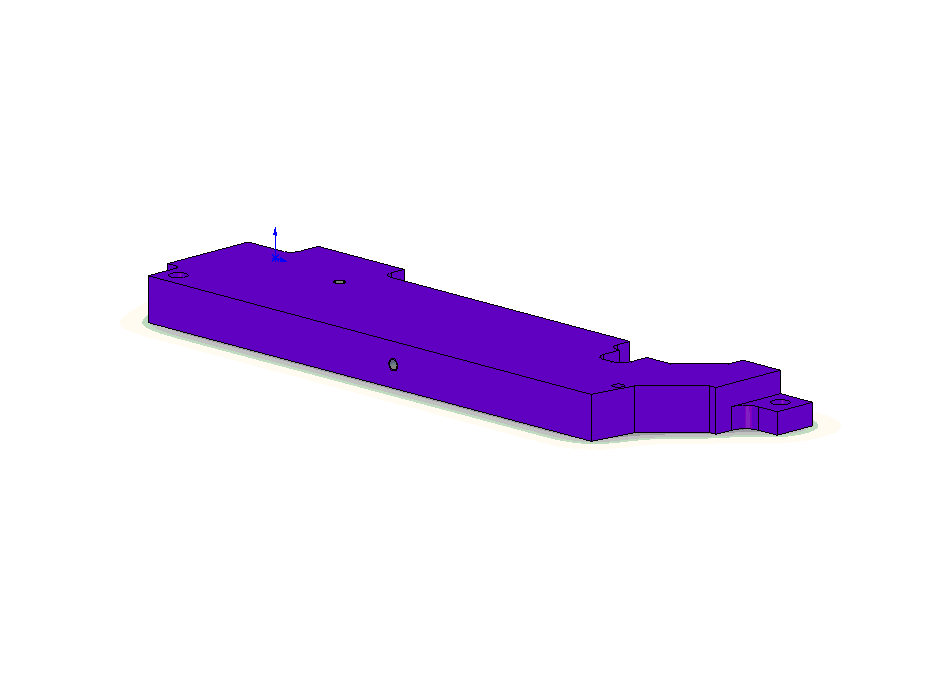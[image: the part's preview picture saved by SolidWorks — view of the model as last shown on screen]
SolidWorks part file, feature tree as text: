
SOLIDWORKS PART (.sldprt)
format: sldprt  version: not decoded by parser v0  size: 1,095,680 bytes
history: native  units: mm
features: sketch x17, cut_extrude x8, hole x4, thread x3, material x1, extrude x1, fillet x1 (+12 scaffold rows collapsed)
feature tree (47):
  scaffold x12  (default folders/planes/origin — collapsed)
  material  "Material <not specified>"
  sketch  "Sketch1"  dims[D1=16.0mm D2=250.0mm D3=~250.008967mm]
  extrude  "Base-Extrude"  Depth=65mm
  sketch  "Sketch3"  dims[c1.D3=20.0mm c1.D4=4.0mm c1.D6=4.0mm c1.D1=15.0mm c1.D2=60.0mm c2.D1=45.0mm c2.D2=18.0mm c3.D1=45.0mm c3.D3=28.0mm c3.D4=15.0mm c4.D1=7.0mm c4.D4=65.0mm c5.D1=~29.08854mm c6.D1=6.0deg c6.D2=16.0mm c6.D4=15.0mm c6.D5=34.595mm c6.D6=435.0mm c6.D7=~364.989602mm c7.D2=400.0mm c7.D7=30.0mm c7.D1=400.0mm c8.D1=~8.616174deg c9.D1=435.0mm c10.D1=8.5deg c11.D1=~45.694142mm c12.D1=81.5deg c12.D2=38.0mm c12.D3=35.0mm c12.D4=18.0mm c12.D5=~25.347536mm c13.D5=45.0deg]
  cut_extrude  "Access for Blade Clamp Bolts"  [1 undecoded]
  sketch  "Sketch6"  dims[c1.D5=4.0mm c1.D6=4.0mm c1.D1=100.0mm c1.D2=10.0mm c1.D3=~45.280213mm c2.D3=90.0deg c3.D3=10.0mm c3.D4=40.0mm c3.D5=20.0mm c4.D3=40.0mm c4.D4=10.0mm]
  cut_extrude  "Cut-Extrude2"  [1 undecoded]
  sketch  "Sketch7"  dims[c1.D2=4.0mm c1.D4=4.0mm c2.D2=4.0mm c2.D1=32.5mm c2.D3=10.0mm c2.D4=~35.410935mm c2.D5=42.5mm c2.D6=~16.138316mm c3.D6=45.0deg c3.D7=5.0mm c3.D2=29.0mm]
  cut_extrude  "Cut-Extrude3"  [1 undecoded]
  hole  "1/4 Clearance Hole1"  Diameter=6.5278mm Depth=16mm
  sketch  "3DSketch2"  dims[c1.D1=7.5mm c1.D2=~9.694641mm c1.D7=7.5mm c1.D3=12.5mm c1.D4=12.5mm c1.D5=6.0mm c1.D6=7.5mm c2.D2=7.5mm c2.D7=7.5mm c2.D8=7.5mm]
  sketch  "Sketch10"  dims[hole-wizard template sketch: 60 standard entries collapsed; hole parameters kept: c18.Thru Hole Depth=16.0mm]
  sketch  "Sketch11"  dims[D3=2.0mm D4=2.0mm D1=6.0mm D2=12.5mm D5=6.0mm D6=15.0mm]
  cut_extrude  "Cut-Extrude4"  [1 undecoded]
  sketch  "Sketch12"  dims[D2=4.0mm D1=20.0mm]
  cut_extrude  "Cut-Extrude5"  Depth=8mm
  hole  "#8-32 Tapped Hole1"  Diameter=3.4544mm Depth=16mm
  sketch  "3DSketch3"  dims[D1=39.0mm D2=194.0mm]
  sketch  "Sketch13"  dims[hole-wizard template sketch: 60 standard entries collapsed; hole parameters kept: c18.Thru Tap Drill Depth=16.0mm]
  thread  "Cosmetic Thread1"  Diameter=8.3312mm  [1 undecoded]
  hole  "#8-32 Tapped Hole2"  Diameter=3.4544mm Depth=12.2936mm
  sketch  "Sketch15"  dims[D1=130.0mm D2=8.0mm]
  sketch  "Sketch14"  dims[hole-wizard template sketch: 47 standard entries collapsed; hole parameters kept: c15.Tap Drill Depth=12.2936mm c15.D3=~14.816244mm c15.Drill Angle=118.0deg]
  thread  "Cosmetic Thread2"  Diameter=8.3312mm  [1 undecoded]
  hole  "#8-32 Tapped Hole3"  Diameter=3.4544mm Depth=16mm
  sketch  "Sketch18"  dims[D1=38.1mm D2=63.5mm]
  sketch  "Sketch19"  dims[hole-wizard template sketch: 60 standard entries collapsed; hole parameters kept: c18.Thru Tap Drill Depth=16.0mm]
  thread  "Cosmetic Thread3"  Diameter=8.3312mm  [1 undecoded]
  sketch  "Sketch20"  dims[D1=15.0mm]
  cut_extrude  "Cut-Extrude6"  [1 undecoded]
  sketch  "Sketch22"  dims[D1=6.35mm D2=12.7mm D3=4.85mm]
  cut_extrude  "Cut-Extrude8"  Depth=9.525mm
  sketch  "Sketch23"  dims[D1=12.0mm D2=13.5mm]
  cut_extrude  "Cut-Extrude9"  [1 undecoded]
  fillet  "Fillet1"  Radius=4.5mm
decode coverage: 28 of 34 modeling features carry decoded parameters
note: ~ marks probable driven/reference dimensions
note: 9 parameter values undecoded
summary: no parameter record found for 6 features; Diameter pulled from absorbed wizard sketch
note: suppression state not decoded; provenance and decode notes live in map.json
